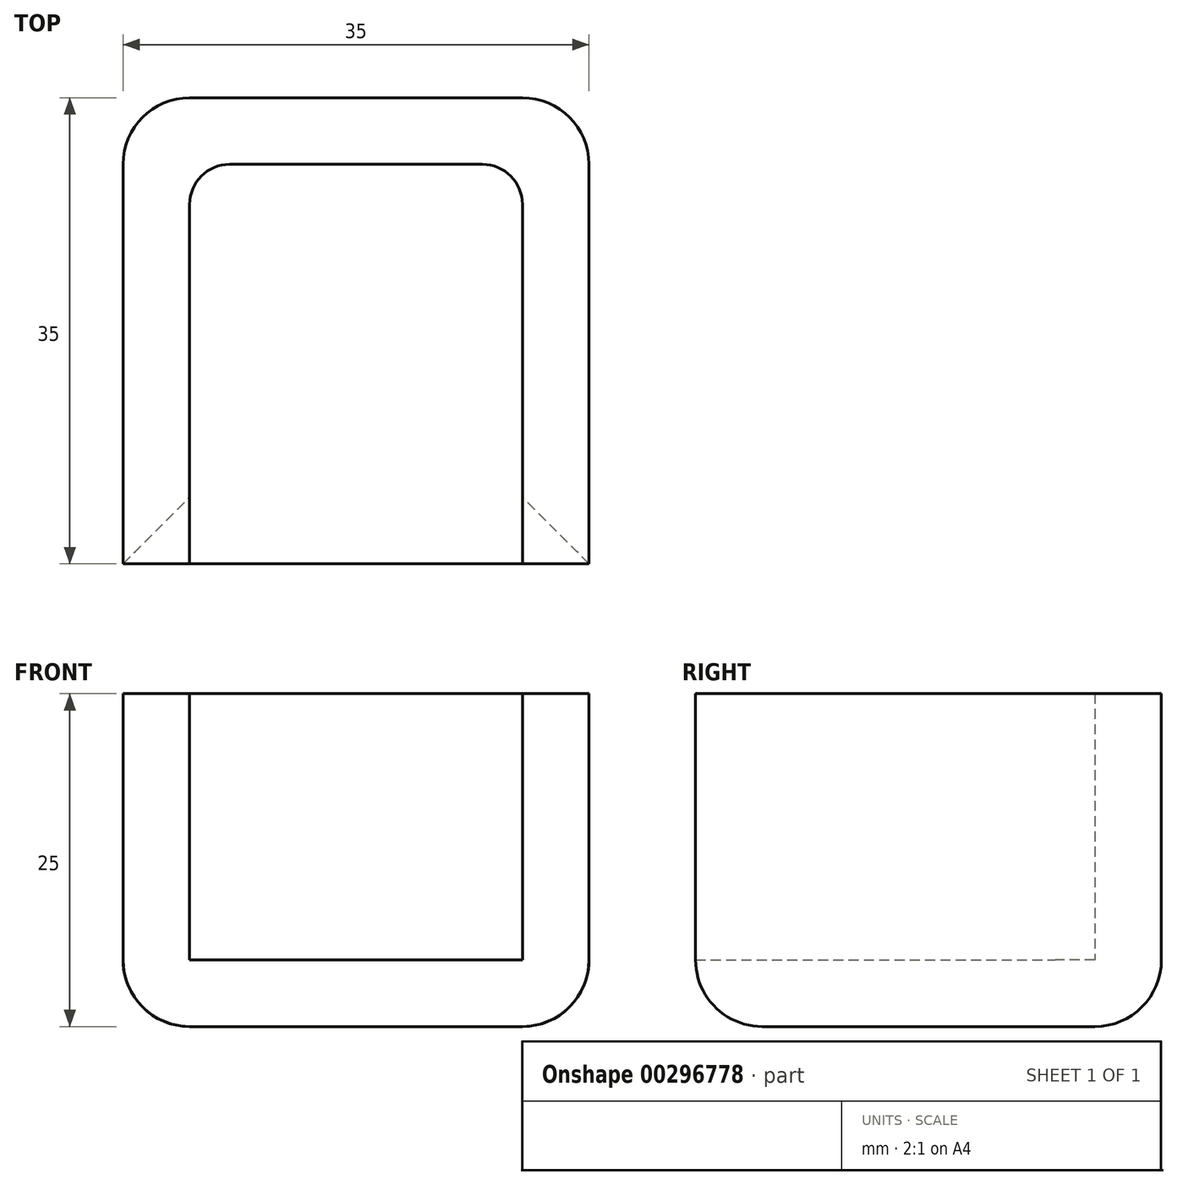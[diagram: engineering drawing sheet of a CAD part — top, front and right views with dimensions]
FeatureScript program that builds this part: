
annotation { "Feature Type Name" : "Feature", "Feature Type Description" : "" }
export const myFeature = defineFeature(function(context is Context, id is Id, definition is map)
    precondition{}
    {
        {
            var Q0;
            Q0=qCreatedBy(makeId("Top.planeOp"),FACE);
            var sketch = newSketch(context, id + "F0", { "sketchPlane" : qUnion([Q0])});
            skLineSegment(sketch, "E0.bottom", {"start": v(17.5, -17.5) * mm, "end": v(-17.5, -17.5) * mm});
            skLineSegment(sketch, "E0.top", {"start": v(12.5, 17.5) * mm, "end": v(-12.5, 17.5) * mm});
            skLineSegment(sketch, "E0.left", {"start": v(17.5, -17.5) * mm, "end": v(17.5, 12.5) * mm});
            skLineSegment(sketch, "E0.right", {"start": v(-17.5, -17.5) * mm, "end": v(-17.5, 12.5) * mm});
            skPoint(sketch, "E0.middle", {"position": v(0, 0) * mm});
            skPoint(sketch, "E1.visualSharp", {"position": v(-17.5, 17.5) * mm});
            skArc(sketch, "E1.filletArc", {"start": v(-12.5, 17.5) * mm, "mid": v(-16.04, 16.04) * mm, "end": v(-17.5, 12.5) * mm});
            skPoint(sketch, "E2.visualSharp", {"position": v(17.5, 17.5) * mm});
            skArc(sketch, "E2.filletArc", {"start": v(17.5, 12.5) * mm, "mid": v(16.04, 16.04) * mm, "end": v(12.5, 17.5) * mm});
            skLineSegment(sketch, "E3.0", {"start": v(12.5, -17.5) * mm, "end": v(12.5, 12.5) * mm});
            skLineSegment(sketch, "E3.1", {"start": v(12.5, 12.5) * mm, "end": v(-12.5, 12.5) * mm});
            skLineSegment(sketch, "E3.2", {"start": v(-12.5, -17.5) * mm, "end": v(-12.5, 12.5) * mm});
            skSolve(sketch);
        }
        {
            var Q0;
            Q0=makeQuery(id+"F0.imprint","IMPRINT",FACE,{"disambiguationData":[TD([[makeQuery(id+"F0.imprint","IMPRINT",EDGE,{"derivedFrom":sQuery(id+"F0.wireOp",EDGE,"E0.top")}),1.0]])]});
            extrude(context, id + "F1", {"entities" : qUnion([Q0]), "depth" : 20 * mm});
        }
        {
            var Q0;
            {var subQ0=sQuery(id+"F0.wireOp",EDGE,"E3.0");Q0=makeQuery(id+"F0.imprint","IMPRINT",FACE,{"disambiguationData":[TD([[makeQuery(id+"F0.imprint","IMPRINT",EDGE,{"derivedFrom":subQ0}),1.0]])]});}
            var Q1;
            Q1=makeQuery(id+"F0.imprint","IMPRINT",FACE,{"disambiguationData":[TD([[makeQuery(id+"F0.imprint","IMPRINT",EDGE,{"derivedFrom":sQuery(id+"F0.wireOp",EDGE,"E0.top")}),1.0]])]});
            extrude(context, id + "F2", {"entities" : qUnion([Q0, Q1]), "operationType" : NewBodyOperationType.ADD, "oppositeDirection" : true, "depth" : 5 * mm});
        }
        {
            var Q0;
            Q0=makeQuery(id+"F2.opExtrude","CAP_FACE",FACE,{"disambiguationData":[OSD([sQuery(id+"F0.wireOp",EDGE,"E0.bottom"),sQuery(id+"F0.wireOp",EDGE,"E0.top"),sQuery(id+"F0.wireOp",EDGE,"E0.left"),sQuery(id+"F0.wireOp",EDGE,"E0.right"),sQuery(id+"F0.wireOp",EDGE,"E1.filletArc"),sQuery(id+"F0.wireOp",EDGE,"E2.filletArc")])],"isStart":false});
            fillet(context, id + "F3", {"entities" : qUnion([Q0]), "radius" : 5 * mm, "tangentPropagation" : true, "allowEdgeOverflow" : false});
        }
        {
            var Q0;
            Q0=makeQuery(id+"F1.opExtrude","CAP_EDGE",EDGE,{"disambiguationData":[OSD([sQuery(id+"F0.wireOp",EDGE,"E3.0")])],"isStart":true});
            var Q1;
            Q1=makeQuery(id+"F1.opExtrude","CAP_EDGE",EDGE,{"disambiguationData":[OSD([sQuery(id+"F0.wireOp",EDGE,"E3.2")])],"isStart":true});
            var Q2;
            Q2=makeQuery(id+"F1.opExtrude","SWEPT_EDGE",EDGE,{"disambiguationData":[OSD([sQuery(id+"F0.wireOp",EDGE,"E3.0"),sQuery(id+"F0.wireOp",EDGE,"E3.1")])]});
            var Q3;
            Q3=makeQuery(id+"F1.opExtrude","SWEPT_EDGE",EDGE,{"disambiguationData":[OSD([sQuery(id+"F0.wireOp",EDGE,"E3.1"),sQuery(id+"F0.wireOp",EDGE,"E3.2")])]});
            var Q4;
            Q4=makeQuery(id+"F1.opExtrude","CAP_EDGE",EDGE,{"disambiguationData":[OSD([sQuery(id+"F0.wireOp",EDGE,"E3.1")])],"isStart":true});
            fillet(context, id + "F4", {"entities" : qUnion([Q0, Q1, Q2, Q3, Q4]), "radius" : 3 * mm, "tangentPropagation" : true, "allowEdgeOverflow" : false});
        }
    });
